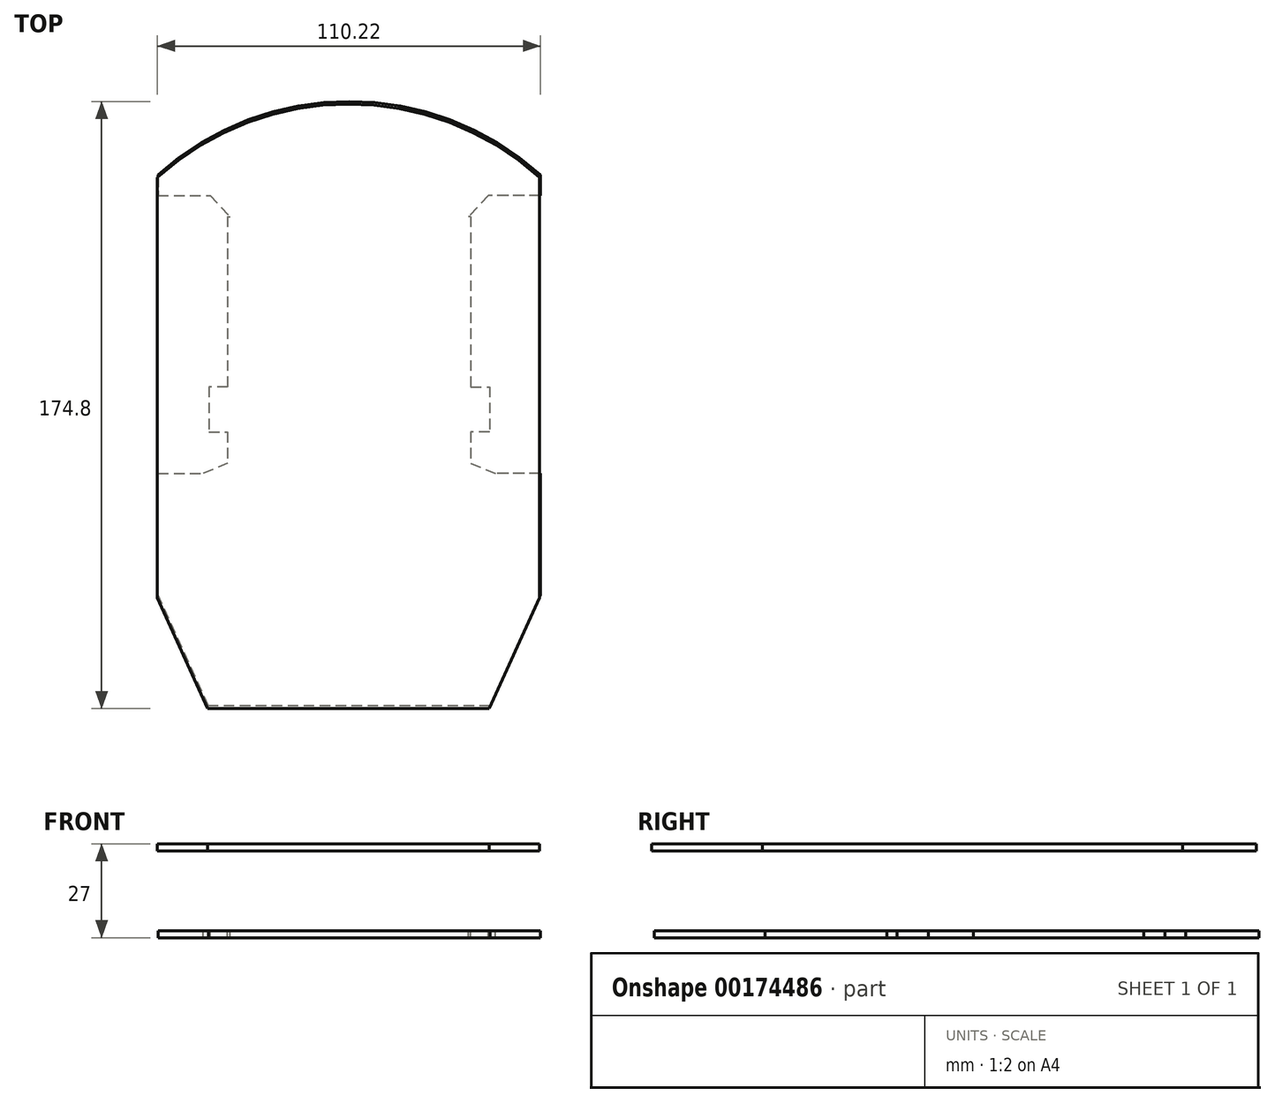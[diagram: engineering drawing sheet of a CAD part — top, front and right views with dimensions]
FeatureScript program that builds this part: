
annotation { "Feature Type Name" : "Feature", "Feature Type Description" : "" }
export const myFeature = defineFeature(function(context is Context, id is Id, definition is map)
    precondition{}
    {
        {
            var Q0;
            Q0=qCreatedBy(makeId("Top.planeOp"),FACE);
            var sketch = newSketch(context, id + "F0", { "sketchPlane" : qUnion([Q0])});
            skLineSegment(sketch, "E0", {"start": v(0, 0) * mm, "end": v(0, -87) * mm, "construction": true});
            skLineSegment(sketch, "E1.MirrorCS", {"start": v(0, 0) * mm, "end": v(0, 87) * mm, "construction": true});
            skLineSegment(sketch, "E2", {"start": v(0, -87) * mm, "end": v(-40.5, -87) * mm});
            skLineSegment(sketch, "E3", {"start": v(-40.5, -87) * mm, "end": v(-55, -55.14) * mm});
            skLineSegment(sketch, "E4", {"start": v(-55, -55.14) * mm, "end": v(-55, 65.86) * mm, "construction": true});
            skLineSegment(sketch, "E5.MirrorCS", {"start": v(0, -87) * mm, "end": v(40.5, -87) * mm});
            skLineSegment(sketch, "E6.MirrorCS", {"start": v(40.5, -87) * mm, "end": v(55, -55.14) * mm});
            skLineSegment(sketch, "E7.MirrorCS", {"start": v(55, -55.14) * mm, "end": v(55, 65.86) * mm, "construction": true});
            skArc(sketch, "E8", {"start": v(55, 65.86) * mm, "mid": v(0, 87) * mm, "end": v(-55, 65.86) * mm});
            skLineSegment(sketch, "E9", {"start": v(-55, -55.14) * mm, "end": v(-55, -20.14) * mm});
            skLineSegment(sketch, "E10", {"start": v(-55, -20.14) * mm, "end": v(-42, -20.14) * mm});
            skLineSegment(sketch, "E11", {"start": v(-55, 65.86) * mm, "end": v(-55, 59.86) * mm});
            skLineSegment(sketch, "E12", {"start": v(-55, 59.86) * mm, "end": v(-40.01, 59.86) * mm});
            skLineSegment(sketch, "E13", {"start": v(-40.01, 59.86) * mm, "end": v(-34.32, 53.82) * mm});
            skLineSegment(sketch, "E14", {"start": v(-35, 53.82) * mm, "end": v(-34.32, 53.82) * mm});
            skLineSegment(sketch, "E15", {"start": v(-35, 53.82) * mm, "end": v(-35, 4.82) * mm});
            skLineSegment(sketch, "E16", {"start": v(-35, 4.82) * mm, "end": v(-40.35, 4.82) * mm});
            skLineSegment(sketch, "E17", {"start": v(-40.35, 4.82) * mm, "end": v(-40.35, -8.18) * mm});
            skLineSegment(sketch, "E18", {"start": v(-40.35, -8.18) * mm, "end": v(-35, -8.18) * mm});
            skLineSegment(sketch, "E19", {"start": v(-35, -8.18) * mm, "end": v(-35, -17.19) * mm});
            skLineSegment(sketch, "E20", {"start": v(-35, -17.19) * mm, "end": v(-42, -20.14) * mm});
            skLineSegment(sketch, "E21.MirrorCS", {"start": v(35, -8.18) * mm, "end": v(35, -17.19) * mm});
            skLineSegment(sketch, "E22.MirrorCS", {"start": v(40.01, 59.86) * mm, "end": v(34.32, 53.82) * mm});
            skLineSegment(sketch, "E23.MirrorCS", {"start": v(35, 53.82) * mm, "end": v(34.32, 53.82) * mm});
            skLineSegment(sketch, "E24.MirrorCS", {"start": v(55, 65.86) * mm, "end": v(55, 59.86) * mm});
            skLineSegment(sketch, "E25.MirrorCS", {"start": v(35, -17.19) * mm, "end": v(42, -20.14) * mm});
            skLineSegment(sketch, "E26.MirrorCS", {"start": v(35, 4.82) * mm, "end": v(40.35, 4.82) * mm});
            skLineSegment(sketch, "E27.MirrorCS", {"start": v(40.35, -8.18) * mm, "end": v(35, -8.18) * mm});
            skLineSegment(sketch, "E28.MirrorCS", {"start": v(55, -55.14) * mm, "end": v(55, -20.14) * mm});
            skLineSegment(sketch, "E29.MirrorCS", {"start": v(35, 53.82) * mm, "end": v(35, 4.82) * mm});
            skArc(sketch, "E30.MirrorCS", {"start": v(-55, 65.86) * mm, "mid": v(0, 87) * mm, "end": v(55, 65.86) * mm});
            skLineSegment(sketch, "E31.MirrorCS", {"start": v(55, -20.14) * mm, "end": v(42, -20.14) * mm});
            skLineSegment(sketch, "E32.MirrorCS", {"start": v(55, 59.86) * mm, "end": v(40.01, 59.86) * mm});
            skLineSegment(sketch, "E33.MirrorCS", {"start": v(40.35, 4.82) * mm, "end": v(40.35, -8.18) * mm});
            skSolve(sketch);
        }
        {
            var Q0;
            Q0=qCreatedBy(makeId("Top.planeOp"),FACE);
            var sketch = newSketch(context, id + "F1", { "sketchPlane" : qUnion([Q0])});
            skLineSegment(sketch, "E34", {"start": v(-0.22, -1.35) * mm, "end": v(-0.22, -87.8) * mm, "construction": true});
            skLineSegment(sketch, "E35.MirrorCS", {"start": v(-0.22, -0.8) * mm, "end": v(-0.22, 86.2) * mm, "construction": true});
            skLineSegment(sketch, "E36", {"start": v(-0.22, -87.8) * mm, "end": v(-40.72, -87.8) * mm});
            skLineSegment(sketch, "E37", {"start": v(-40.72, -87.8) * mm, "end": v(-55.22, -55.95) * mm});
            skLineSegment(sketch, "E38", {"start": v(-55.22, -55.95) * mm, "end": v(-55.22, 65.05) * mm});
            skLineSegment(sketch, "E39.MirrorCS", {"start": v(-0.22, -87.8) * mm, "end": v(40.28, -87.8) * mm});
            skLineSegment(sketch, "E40.MirrorCS", {"start": v(40.28, -87.8) * mm, "end": v(54.78, -55.95) * mm});
            skLineSegment(sketch, "E41.MirrorCS", {"start": v(54.78, -55.95) * mm, "end": v(54.78, 65.05) * mm});
            skArc(sketch, "E42", {"start": v(54.78, 65.05) * mm, "mid": v(-0.22, 86.2) * mm, "end": v(-55.22, 65.05) * mm});
            skSolve(sketch);
        }
        {
            var Q0;
            Q0 = qSketchRegion(id + "F1", true);
            extrude(context, id + "F2", {"entities" : qUnion([Q0]), "depth" : 25 * mm});
        }
        {
            var Q0;
            Q0 = qSketchRegion(id + "F1", true);
            extrude(context, id + "F3", {"entities" : qUnion([Q0]), "operationType" : NewBodyOperationType.REMOVE, "depth" : 23 * mm});
        }
        {
            var Q0;
            Q0 = qSketchRegion(id + "F0", true);
            extrude(context, id + "F4", {"entities" : qUnion([Q0]), "oppositeDirection" : true, "depth" : 2 * mm});
        }
    });
